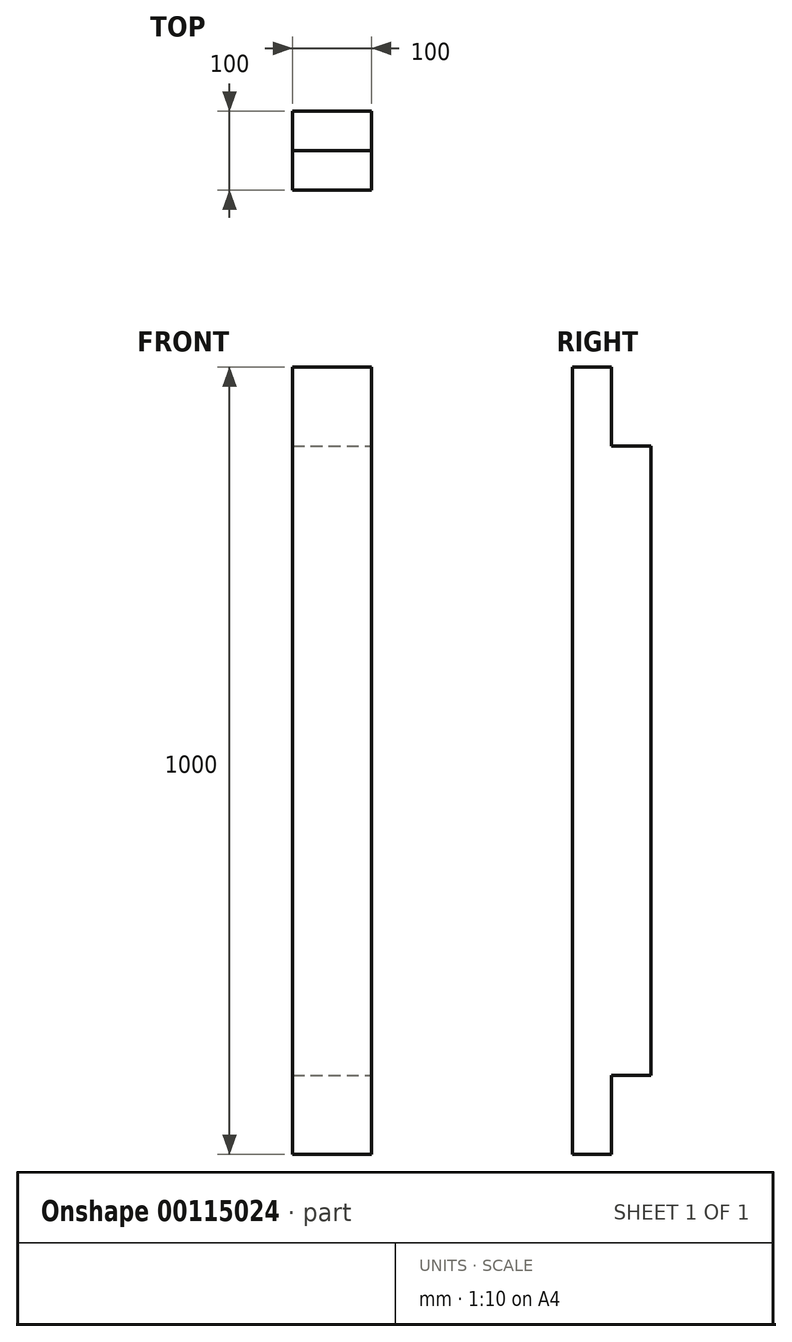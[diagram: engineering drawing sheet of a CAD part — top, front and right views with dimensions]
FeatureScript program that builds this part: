
annotation { "Feature Type Name" : "Feature", "Feature Type Description" : "" }
export const myFeature = defineFeature(function(context is Context, id is Id, definition is map)
    precondition{}
    {
        {
            var Q0;
            Q0=qCreatedBy(makeId("Top.planeOp"),FACE);
            var sketch = newSketch(context, id + "F0", { "sketchPlane" : qUnion([Q0])});
            skLineSegment(sketch, "E0.bottom", {"start": v(50, -50) * mm, "end": v(-50, -50) * mm});
            skLineSegment(sketch, "E0.top", {"start": v(50, 50) * mm, "end": v(-50, 50) * mm});
            skLineSegment(sketch, "E0.left", {"start": v(50, -50) * mm, "end": v(50, 50) * mm});
            skLineSegment(sketch, "E0.right", {"start": v(-50, -50) * mm, "end": v(-50, 50) * mm});
            skPoint(sketch, "E0.middle", {"position": v(0, 0) * mm});
            skSolve(sketch);
        }
        {
            var Q0;
            Q0=qSketchRegion(id+"F0",true);
            extrude(context, id + "F1", {"entities" : qUnion([Q0]), "depth" : 1000 * mm});
        }
        {
            var Q0;
            Q0=makeQuery(id+"F1.opExtrude","SWEPT_FACE",FACE,{"disambiguationData":[OSD([sQuery(id+"F0.wireOp",EDGE,"E0.left")])]});
            var sketch = newSketch(context, id + "F2", { "sketchPlane" : qUnion([Q0])});
            skLineSegment(sketch, "E1.bottom", {"start": v(0, 0) * mm, "end": v(50, 0) * mm});
            skLineSegment(sketch, "E1.top", {"start": v(0, 100) * mm, "end": v(50, 100) * mm});
            skLineSegment(sketch, "E1.left", {"start": v(0, 0) * mm, "end": v(0, 100) * mm});
            skLineSegment(sketch, "E1.right", {"start": v(50, 0) * mm, "end": v(50, 100) * mm});
            skLineSegment(sketch, "E2.bottom", {"start": v(0, 1000) * mm, "end": v(50, 1000) * mm});
            skLineSegment(sketch, "E2.top", {"start": v(0, 900) * mm, "end": v(50, 900) * mm});
            skLineSegment(sketch, "E2.left", {"start": v(50, 1000) * mm, "end": v(50, 900) * mm});
            skLineSegment(sketch, "E2.right", {"start": v(0, 1000) * mm, "end": v(0, 900) * mm});
            skSolve(sketch);
        }
        {
            var Q0;
            Q0 = qSketchRegion(id + "F2", true);
            extrude(context, id + "F3", {"entities" : qUnion([Q0]), "operationType" : NewBodyOperationType.REMOVE, "endBound" : BoundingType.THROUGH_ALL, "oppositeDirection" : true, "depth" : 25 * mm});
        }
    });
